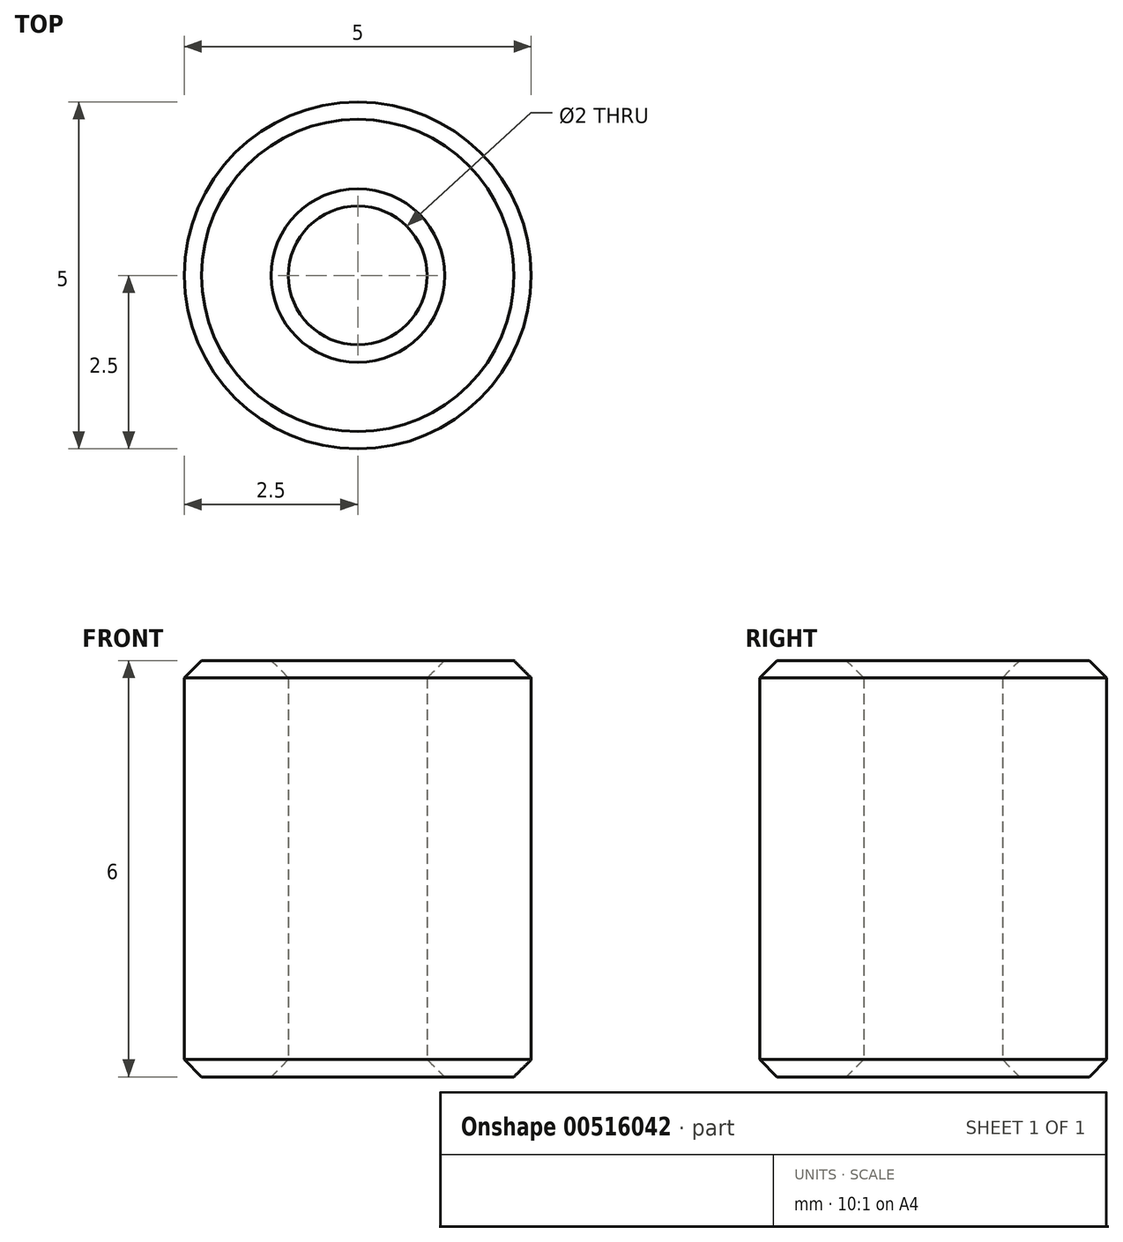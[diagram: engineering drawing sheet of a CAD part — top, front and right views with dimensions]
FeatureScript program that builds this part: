
annotation { "Feature Type Name" : "Feature", "Feature Type Description" : "" }
export const myFeature = defineFeature(function(context is Context, id is Id, definition is map)
    precondition{}
    {
        {
            var Q0;
            Q0=qCreatedBy(makeId("Top.planeOp"),FACE);
            var sketch = newSketch(context, id + "F0", { "sketchPlane" : qUnion([Q0])});
            skCircle(sketch, "E0", {"center": v(0, 0) * mm, "radius": 2.5 * mm});
            skCircle(sketch, "E1", {"center": v(0, 0) * mm, "radius": 1 * mm});
            skSolve(sketch);
        }
        {
            var Q0;
            Q0 = qSketchRegion(id + "F0", true);
            extrude(context, id + "F1", {"entities" : qUnion([Q0]), "depth" : 6 * mm, "offsetDistance" : 25 * mm});
        }
        {
            var Q0;
            Q0=makeQuery(id+"F1.opExtrude","CAP_EDGE",EDGE,{"disambiguationData":[OSD([sQuery(id+"F0.wireOp",EDGE,"E0")])],"isStart":false});
            var Q1;
            Q1=makeQuery(id+"F1.opExtrude","CAP_EDGE",EDGE,{"disambiguationData":[OSD([sQuery(id+"F0.wireOp",EDGE,"E0")])],"isStart":true});
            var Q2;
            Q2=makeQuery(id+"F1.opExtrude","CAP_EDGE",EDGE,{"disambiguationData":[OSD([sQuery(id+"F0.wireOp",EDGE,"E1")])],"isStart":false});
            var Q3;
            Q3=makeQuery(id+"F1.opExtrude","CAP_EDGE",EDGE,{"disambiguationData":[OSD([sQuery(id+"F0.wireOp",EDGE,"E1")])],"isStart":true});
            chamfer(context, id + "F2", {"entities" : qUnion([Q0, Q1, Q2, Q3]), "width" : .25 * mm, "tangentPropagation" : true});
        }
    });
